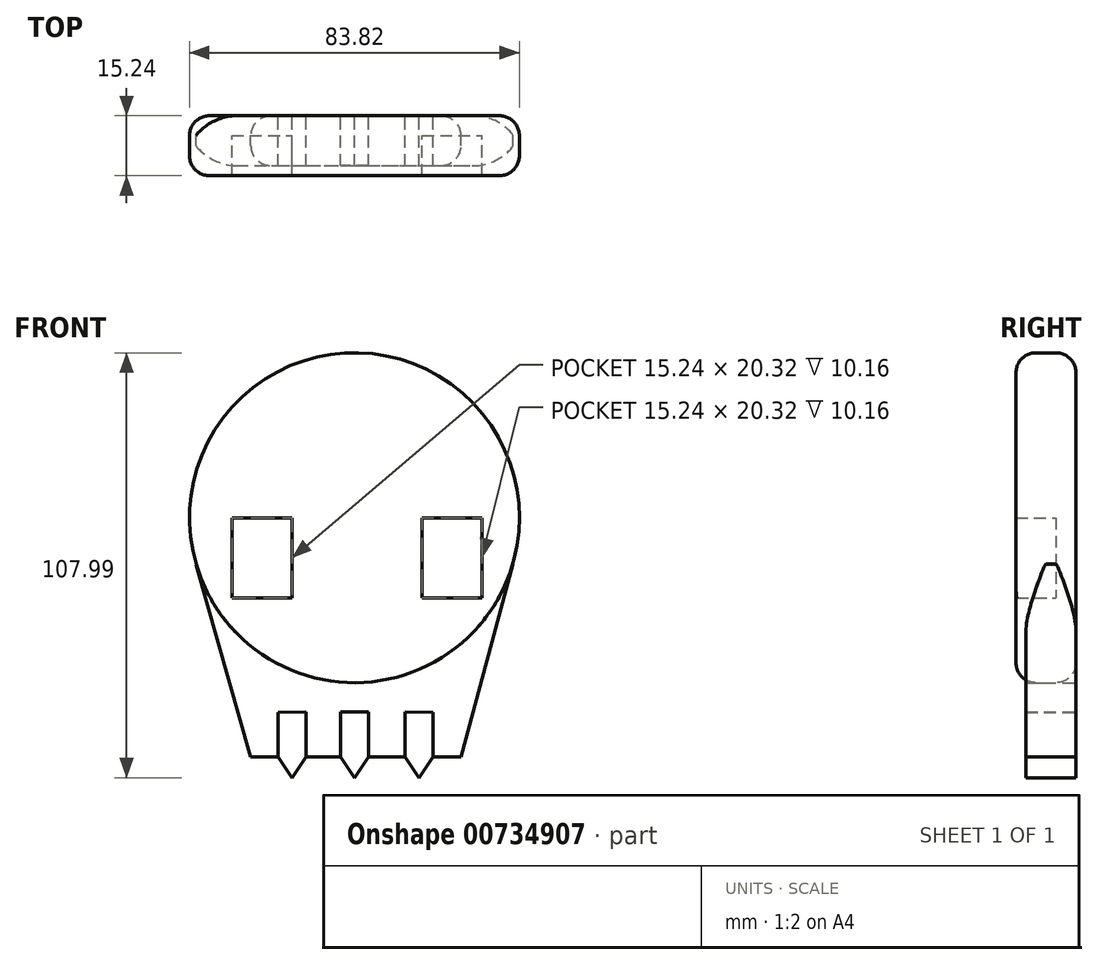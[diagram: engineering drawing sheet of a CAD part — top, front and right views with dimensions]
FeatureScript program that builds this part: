
annotation { "Feature Type Name" : "Feature", "Feature Type Description" : "" }
export const myFeature = defineFeature(function(context is Context, id is Id, definition is map)
    precondition{}
    {
        {
            var Q0;
            Q0=qCreatedBy(makeId("Front.planeOp"),FACE);
            var sketch = newSketch(context, id + "F0", { "sketchPlane" : qUnion([Q0])});
            skCircle(sketch, "E0", {"center": v(0, 0) * mm, "radius": 41.91 * mm});
            skLineSegment(sketch, "E1", {"start": v(-40.17, -11.94) * mm, "end": v(-26.33, -60.82) * mm});
            skLineSegment(sketch, "E2", {"start": v(27.07, -60.82) * mm, "end": v(40.23, -11.75) * mm});
            skLineSegment(sketch, "E3", {"start": v(-12.33, -60.82) * mm, "end": v(-12.33, -49.39) * mm});
            skLineSegment(sketch, "E4", {"start": v(12.8, -60.82) * mm, "end": v(12.8, -49.39) * mm});
            skLineSegment(sketch, "E5", {"start": v(3.56, -60.82) * mm, "end": v(3.56, -49.39) * mm});
            skLineSegment(sketch, "E6", {"start": v(-3.56, -60.82) * mm, "end": v(-3.56, -49.39) * mm});
            skLineSegment(sketch, "E7.bottom", {"start": v(-31.14, 0) * mm, "end": v(-15.9, 0) * mm});
            skLineSegment(sketch, "E7.top", {"start": v(-31.14, -20.32) * mm, "end": v(-15.9, -20.32) * mm});
            skLineSegment(sketch, "E7.left", {"start": v(-31.14, 0) * mm, "end": v(-31.14, -20.32) * mm});
            skLineSegment(sketch, "E7.right", {"start": v(-15.9, 0) * mm, "end": v(-15.9, -20.32) * mm});
            skLineSegment(sketch, "E8.bottom", {"start": v(17.23, 0) * mm, "end": v(32.47, 0) * mm});
            skLineSegment(sketch, "E8.top", {"start": v(17.23, -20.32) * mm, "end": v(32.47, -20.32) * mm});
            skLineSegment(sketch, "E8.left", {"start": v(17.23, 0) * mm, "end": v(17.23, -20.32) * mm});
            skLineSegment(sketch, "E8.right", {"start": v(32.47, 0) * mm, "end": v(32.47, -20.32) * mm});
            skLineSegment(sketch, "E9", {"start": v(-19.44, -60.82) * mm, "end": v(-19.44, -49.5) * mm});
            skLineSegment(sketch, "E10", {"start": v(19.9, -60.82) * mm, "end": v(19.9, -49.5) * mm});
            skLineSegment(sketch, "E11", {"start": v(-19.44, -49.5) * mm, "end": v(-12.33, -49.39) * mm});
            skLineSegment(sketch, "E12", {"start": v(12.8, -49.39) * mm, "end": v(19.9, -49.5) * mm});
            skLineSegment(sketch, "E13", {"start": v(3.56, -49.39) * mm, "end": v(-3.56, -49.39) * mm});
            skLineSegment(sketch, "E14", {"start": v(-19.44, -60.82) * mm, "end": v(-15.88, -66.08) * mm});
            skLineSegment(sketch, "E15", {"start": v(-15.88, -66.08) * mm, "end": v(-12.33, -60.82) * mm});
            skLineSegment(sketch, "E16", {"start": v(-3.56, -60.82) * mm, "end": v(0, -66.08) * mm});
            skLineSegment(sketch, "E17", {"start": v(0, -66.08) * mm, "end": v(3.56, -60.82) * mm});
            skLineSegment(sketch, "E18", {"start": v(12.8, -60.82) * mm, "end": v(16.35, -66.08) * mm});
            skLineSegment(sketch, "E19", {"start": v(16.35, -66.08) * mm, "end": v(19.9, -60.82) * mm});
            skLineSegment(sketch, "E20", {"start": v(-26.33, -60.82) * mm, "end": v(-19.44, -60.82) * mm});
            skLineSegment(sketch, "E21", {"start": v(-12.33, -60.82) * mm, "end": v(-3.56, -60.82) * mm});
            skLineSegment(sketch, "E22", {"start": v(3.56, -60.82) * mm, "end": v(12.8, -60.82) * mm});
            skLineSegment(sketch, "E23", {"start": v(19.9, -60.82) * mm, "end": v(27.07, -60.82) * mm});
            skLineSegment(sketch, "E24", {"start": v(0, 41.91) * mm, "end": v(0, -41.91) * mm});
            skSolve(sketch);
        }
        {
            var Q0;
            Q0=makeQuery(id+"F0.imprint","IMPRINT",FACE,{"disambiguationData":[TD([[makeQuery(id+"F0.imprint","IMPRINT",EDGE,{"derivedFrom":sQuery(id+"F0.wireOp",EDGE,"E3")}),1.0]])]});
            var Q1;
            Q1=makeQuery(id+"F0.imprint","IMPRINT",FACE,{"disambiguationData":[TD([[makeQuery(id+"F0.imprint","IMPRINT",EDGE,{"derivedFrom":sQuery(id+"F0.wireOp",EDGE,"E5")}),1.0]])]});
            var Q2;
            Q2=makeQuery(id+"F0.imprint","IMPRINT",FACE,{"disambiguationData":[TD([[makeQuery(id+"F0.imprint","IMPRINT",EDGE,{"derivedFrom":sQuery(id+"F0.wireOp",EDGE,"E4")}),-1.0]])]});
            extrude(context, id + "F1", {"entities" : qUnion([Q0, Q1, Q2]), "depth" : 12.7 * mm, "offsetDistance" : 25.4 * mm});
        }
        {
            var Q0;
            Q0=makeQuery(id+"F0.imprint","IMPRINT",FACE,{"disambiguationData":[TD([[makeQuery(id+"F0.imprint","IMPRINT",EDGE,{"derivedFrom":sQuery(id+"F0.wireOp",EDGE,"E7.bottom")}),1.0]])]});
            var Q1;
            Q1=makeQuery(id+"F0.imprint","IMPRINT",FACE,{"disambiguationData":[TD([[makeQuery(id+"F0.imprint","IMPRINT",EDGE,{"derivedFrom":sQuery(id+"F0.wireOp",EDGE,"E8.bottom")}),1.0]])]});
            extrude(context, id + "F2", {"entities" : qUnion([Q0, Q1]), "depth" : 15.24 * mm, "offsetDistance" : 25.4 * mm});
        }
        {
            var Q0;
            Q0=makeQuery(id+"F0.imprint","IMPRINT",FACE,{"disambiguationData":[TD([[makeQuery(id+"F0.imprint","IMPRINT",EDGE,{"derivedFrom":sQuery(id+"F0.wireOp",EDGE,"E7.bottom")}),-1.0]])]});
            var Q1;
            Q1=makeQuery(id+"F0.imprint","IMPRINT",FACE,{"disambiguationData":[TD([[makeQuery(id+"F0.imprint","IMPRINT",EDGE,{"derivedFrom":sQuery(id+"F0.wireOp",EDGE,"E8.bottom")}),-1.0]])]});
            extrude(context, id + "F3", {"entities" : qUnion([Q0, Q1]), "operationType" : NewBodyOperationType.ADD, "depth" : 5.08 * mm, "offsetDistance" : 25.4 * mm});
        }
        {
            var Q0;
            Q0=makeQuery(id+"F2.opExtrude","CAP_EDGE",EDGE,{"disambiguationData":[OSD([sQuery(id+"F0.wireOp",EDGE,"E0")])],"isStart":false});
            var Q1;
            Q1=makeQuery(id+"F2.opExtrude","CAP_EDGE",EDGE,{"disambiguationData":[OSD([sQuery(id+"F0.wireOp",EDGE,"E0")])],"isStart":true});
            fillet(context, id + "F4", {"entities" : qUnion([Q0, Q1]), "radius" : 5.08 * mm, "tangentPropagation" : true, "allowEdgeOverflow" : false});
        }
        {
            var Q0;
            {var subQ0=sQuery(id+"F0.wireOp",EDGE,"E1");Q0=makeQuery(id+"F0.imprint","IMPRINT",FACE,{"disambiguationData":[TD([[makeQuery(id+"F0.imprint","IMPRINT",EDGE,{"derivedFrom":subQ0}),1.0]])]});}
            extrude(context, id + "F5", {"entities" : qUnion([Q0]), "depth" : 12.7 * mm, "offsetDistance" : 25.4 * mm});
        }
        {
            var Q0;
            Q0=makeQuery(id+"F5.opExtrude","CAP_EDGE",EDGE,{"disambiguationData":[OSD([sQuery(id+"F0.wireOp",EDGE,"E1")])],"isStart":false});
            var Q1;
            Q1=makeQuery(id+"F5.opExtrude","CAP_EDGE",EDGE,{"disambiguationData":[OSD([sQuery(id+"F0.wireOp",EDGE,"E2")])],"isStart":false});
            var Q2;
            Q2=makeQuery(id+"F5.opExtrude","CAP_EDGE",EDGE,{"disambiguationData":[OSD([sQuery(id+"F0.wireOp",EDGE,"E1")])],"isStart":true});
            var Q3;
            Q3=makeQuery(id+"F5.opExtrude","CAP_EDGE",EDGE,{"disambiguationData":[OSD([sQuery(id+"F0.wireOp",EDGE,"E2")])],"isStart":true});
            fillet(context, id + "F6", {"entities" : qUnion([Q0, Q1, Q2, Q3]), "radius" : 5.08 * mm, "tangentPropagation" : true, "allowEdgeOverflow" : false});
        }
    });
